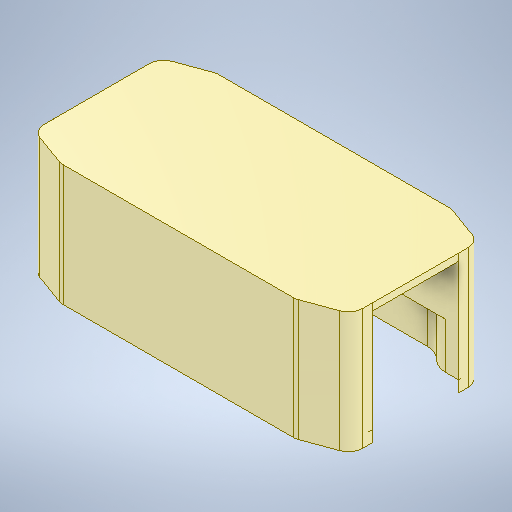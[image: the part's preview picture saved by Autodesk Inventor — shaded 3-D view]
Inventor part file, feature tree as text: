
AUTODESK INVENTOR PART (.ipt)
format: ipt  version: 2025.1 (Build 291241020, 241B)  size: 429,056 bytes
history: native  units: mm
features: extrude x6, sketch x5, projected_geometry x4
ambient origin geometry x8: Origin, YZ Plane, XZ Plane, XY Plane, X Axis, Y Axis, Z Axis, Center Point
bodies: Solid1 (feature_tree)
feature tree (15):
  sketch  "Sketch1"  dims[d0=14.5mm d1=0.0mm d2=1.6mm d3=0.0mm]
  extrude  "Extrusion1"  Depth=1.6mm TaperAngle=0.0deg
  extrude  "Extrusion2"  Depth=0.4mm
  extrude  "Extrusion3"  Depth=1.0mm TaperAngle=0.0deg
  extrude  "Extrusion4"  Depth=3.6mm TaperAngle=0.0deg
  extrude  "Extrusion5"  Depth=8.0mm TaperAngle=0.0deg
  extrude  "Extrusion6"  Depth=2.0mm
  sketch  "Sketch3"  dims[d4=0.4mm d6=0.4mm]
  sketch  "Sketch4"  dims[d8=8.0mm d9=0.0mm d10=1.0mm d11=0.0mm]
  projected_geometry  "Projected Loop1"
  projected_geometry  "Projected Loop2"
  sketch  "Sketch5"  dims[d13=16.6mm d14=3.6mm d15=0.0mm]
  projected_geometry  "Projected Loop3"
  sketch  "Sketch6"  dims[d16=13.6mm d17=8.0mm d18=0.0mm d19=2.0mm d20=2.0mm d33=1.0mm d34=1.0mm d35=0.5mm d36=0.872665mm d37=0.5mm d38=0.872665mm]
  projected_geometry  "Projected Loop4"
